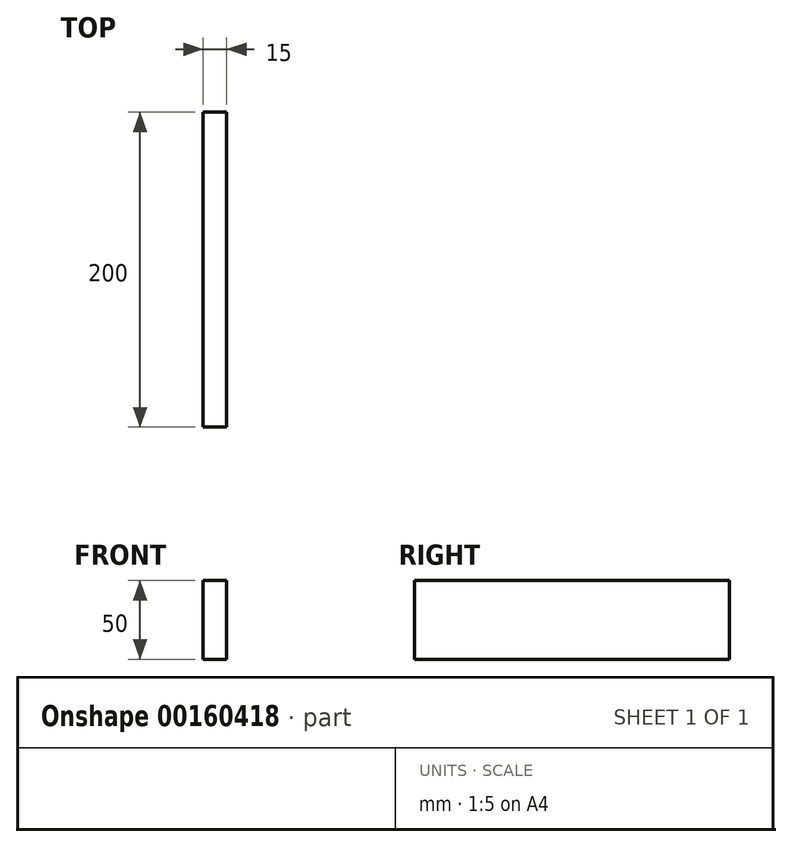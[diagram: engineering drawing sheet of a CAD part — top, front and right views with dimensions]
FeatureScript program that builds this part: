
annotation { "Feature Type Name" : "Feature", "Feature Type Description" : "" }
export const myFeature = defineFeature(function(context is Context, id is Id, definition is map)
    precondition{}
    {
        {
            var Q0;
            Q0=qCreatedBy(makeId("Right.planeOp"),FACE);
            var sketch = newSketch(context, id + "F0", { "sketchPlane" : qUnion([Q0])});
            skLineSegment(sketch, "E0.bottom", {"start": v(-133.33, 50) * mm, "end": v(66.67, 50) * mm});
            skLineSegment(sketch, "E0.top", {"start": v(-133.33, 0) * mm, "end": v(66.67, 0) * mm});
            skLineSegment(sketch, "E0.left", {"start": v(-133.33, 50) * mm, "end": v(-133.33, 0) * mm});
            skLineSegment(sketch, "E0.right", {"start": v(66.67, 50) * mm, "end": v(66.67, 0) * mm});
            skSolve(sketch);
        }
        {
            var Q0;
            Q0=makeQuery(id+"F0.imprint","IMPRINT",FACE,{"disambiguationData":[TD([[makeQuery(id+"F0.imprint","IMPRINT",EDGE,{"derivedFrom":sQuery(id+"F0.wireOp",EDGE,"E0.bottom")}),-1.0]])]});
            extrude(context, id + "F1", {"entities" : qUnion([Q0]), "depth" : 15 * mm});
        }
    });
